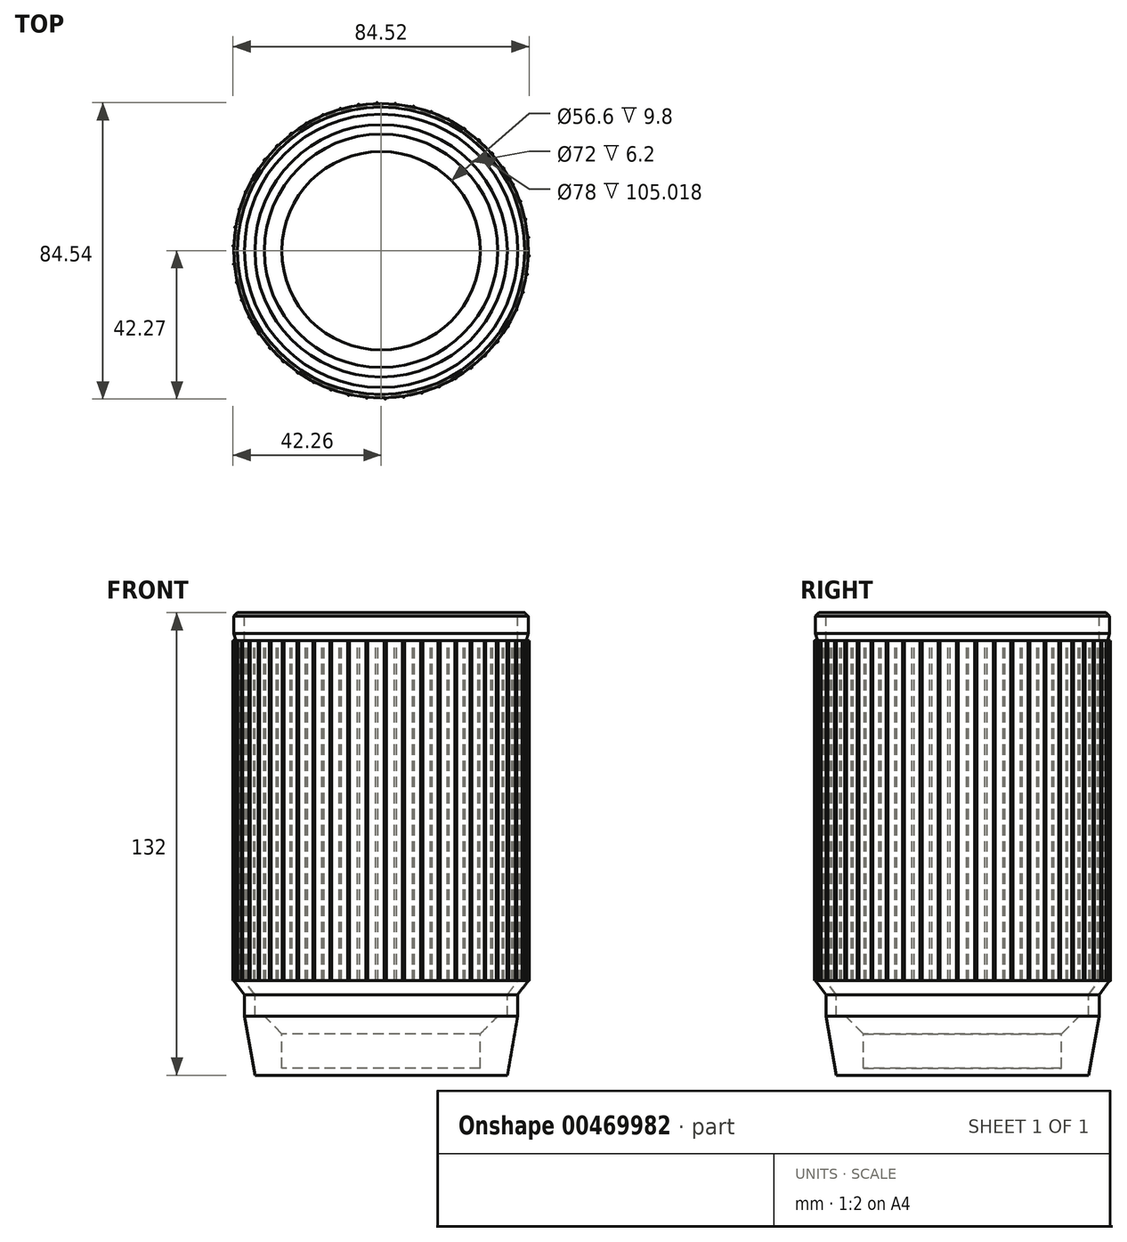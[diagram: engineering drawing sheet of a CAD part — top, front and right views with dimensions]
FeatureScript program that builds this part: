
annotation { "Feature Type Name" : "Feature", "Feature Type Description" : "" }
export const myFeature = defineFeature(function(context is Context, id is Id, definition is map)
    precondition{}
    {
        {
            var Q0;
            Q0=qCreatedBy(makeId("Front.planeOp"),FACE);
            var sketch = newSketch(context, id + "F0", { "sketchPlane" : qUnion([Q0])});
            skLineSegment(sketch, "E0", {"start": v(0, 0) * mm, "end": v(-28.3, 0) * mm});
            skLineSegment(sketch, "E1", {"start": v(-28.3, 0) * mm, "end": v(-28.3, 9.8) * mm});
            skLineSegment(sketch, "E2.bottom", {"start": v(0, 0) * mm, "end": v(-36, 0) * mm, "construction": true});
            skLineSegment(sketch, "E2.top", {"start": v(0, 21) * mm, "end": v(-36, 21) * mm, "construction": true});
            skLineSegment(sketch, "E2.left", {"start": v(0, 0) * mm, "end": v(0, 21) * mm, "construction": true});
            skLineSegment(sketch, "E2.right", {"start": v(-36, 0) * mm, "end": v(-36, 21) * mm, "construction": true});
            skLineSegment(sketch, "E3", {"start": v(-36, 21) * mm, "end": v(-36, 14.8) * mm});
            skLineSegment(sketch, "E4", {"start": v(-36, 14.8) * mm, "end": v(-33.3, 14.8) * mm});
            skLineSegment(sketch, "E5.bottom", {"start": v(0, 0) * mm, "end": v(-39, 0) * mm, "construction": true});
            skLineSegment(sketch, "E5.top", {"start": v(0, 130) * mm, "end": v(-39, 130) * mm, "construction": true});
            skLineSegment(sketch, "E5.left", {"start": v(0, 0) * mm, "end": v(0, 130) * mm, "construction": true});
            skLineSegment(sketch, "E5.right", {"start": v(-39, 0) * mm, "end": v(-39, 130) * mm, "construction": true});
            skLineSegment(sketch, "E6", {"start": v(-36, 21) * mm, "end": v(-39, 24.98) * mm});
            skLineSegment(sketch, "E7", {"start": v(-39, 24.98) * mm, "end": v(-39, 130) * mm});
            skLineSegment(sketch, "E8", {"start": v(-39, 130) * mm, "end": v(-42, 130) * mm});
            skLineSegment(sketch, "E9", {"start": v(-42, 130) * mm, "end": v(-42, 124) * mm});
            skLineSegment(sketch, "E10.bottom", {"start": v(-39, 130) * mm, "end": v(-41.4, 130) * mm, "construction": true});
            skLineSegment(sketch, "E10.top", {"start": v(-39, 122) * mm, "end": v(-41.4, 122) * mm, "construction": true});
            skLineSegment(sketch, "E10.left", {"start": v(-39, 130) * mm, "end": v(-39, 122) * mm, "construction": true});
            skLineSegment(sketch, "E10.right", {"start": v(-41.4, 130) * mm, "end": v(-41.4, 122) * mm, "construction": true});
            skLineSegment(sketch, "E11", {"start": v(-42, 124) * mm, "end": v(-41.4, 122) * mm});
            skLineSegment(sketch, "E12", {"start": v(-42, 122) * mm, "end": v(-42, 24.98) * mm});
            skLineSegment(sketch, "E13", {"start": v(-42, 24.98) * mm, "end": v(-39, 21) * mm});
            skLineSegment(sketch, "E14", {"start": v(-39, 21) * mm, "end": v(-39, 14.8) * mm});
            skLineSegment(sketch, "E15", {"start": v(-36, 17.9) * mm, "end": v(-39, 17.9) * mm, "construction": true});
            skLineSegment(sketch, "E16", {"start": v(0, 0) * mm, "end": v(0, -2) * mm});
            skLineSegment(sketch, "E17", {"start": v(0, -2) * mm, "end": v(-28.3, -2) * mm});
            skLineSegment(sketch, "E18", {"start": v(-39, 14.8) * mm, "end": v(-36, -2) * mm});
            skLineSegment(sketch, "E19", {"start": v(-36, -2) * mm, "end": v(-28.3, -2) * mm});
            skLineSegment(sketch, "E20", {"start": v(-33.3, 14.8) * mm, "end": v(-28.3, 9.8) * mm});
            skLineSegment(sketch, "E21", {"start": v(-42, 122) * mm, "end": v(-41.4, 122) * mm});
            skSolve(sketch);
        }
        {
            var Q0;
            Q0=makeQuery(id+"F0.imprint","IMPRINT",FACE,{"disambiguationData":[TD([[makeQuery(id+"F0.imprint","IMPRINT",EDGE,{"derivedFrom":sQuery(id+"F0.wireOp",EDGE,"E0")}),1.0]])]});
            var Q1;
            Q1=sQuery(id+"F0.wireOp",EDGE,"E16");
            revolve(context, id + "F1", {"entities" : qUnion([Q0]), "axis" : qUnion([Q1]), "revolveType" : RevolveType.FULL});
        }
        {
            var Q0;
            Q0=makeQuery(id+"F1.opRevolve","SWEPT_FACE",FACE,{"disambiguationData":[OSD([sQuery(id+"F0.wireOp",EDGE,"E21")])]});
            var sketch = newSketch(context, id + "F2", { "sketchPlane" : qUnion([Q0])});
            skCircle(sketch, "E22", {"center": v(36.08, -21.5) * mm, "radius": 0.29 * mm});
            skCircle(sketch, "E23.1.0", {"center": v(38.5, -16.8) * mm, "radius": 0.29 * mm});
            skCircle(sketch, "E23.2.0", {"center": v(40.3, -11.84) * mm, "radius": 0.29 * mm});
            skCircle(sketch, "E23.3.0", {"center": v(41.46, -6.7) * mm, "radius": 0.29 * mm});
            skCircle(sketch, "E23.4.0", {"center": v(41.97, -1.45) * mm, "radius": 0.29 * mm});
            skCircle(sketch, "E23.5.0", {"center": v(41.83, 3.82) * mm, "radius": 0.29 * mm});
            skCircle(sketch, "E23.6.0", {"center": v(41.02, 9.03) * mm, "radius": 0.29 * mm});
            skCircle(sketch, "E23.7.0", {"center": v(39.56, 14.1) * mm, "radius": 0.29 * mm});
            skCircle(sketch, "E23.8.0", {"center": v(37.48, 18.95) * mm, "radius": 0.29 * mm});
            skCircle(sketch, "E23.9.0", {"center": v(34.81, 23.5) * mm, "radius": 0.29 * mm});
            skCircle(sketch, "E23.10.0", {"center": v(31.6, 27.68) * mm, "radius": 0.29 * mm});
            skCircle(sketch, "E23.11.0", {"center": v(27.87, 31.42) * mm, "radius": 0.29 * mm});
            skCircle(sketch, "E23.12.0", {"center": v(23.72, 34.66) * mm, "radius": 0.29 * mm});
            skCircle(sketch, "E23.13.0", {"center": v(19.19, 37.36) * mm, "radius": 0.29 * mm});
            skCircle(sketch, "E23.14.0", {"center": v(14.35, 39.47) * mm, "radius": 0.29 * mm});
            skCircle(sketch, "E23.15.0", {"center": v(9.3, 40.96) * mm, "radius": 0.29 * mm});
            skCircle(sketch, "E23.16.0", {"center": v(4.08, 41.8) * mm, "radius": 0.29 * mm});
            skCircle(sketch, "E23.17.0", {"center": v(-1.19, 41.98) * mm, "radius": 0.29 * mm});
            skCircle(sketch, "E23.18.0", {"center": v(-6.44, 41.5) * mm, "radius": 0.29 * mm});
            skCircle(sketch, "E23.19.0", {"center": v(-11.6, 40.37) * mm, "radius": 0.29 * mm});
            skCircle(sketch, "E23.20.0", {"center": v(-16.56, 38.6) * mm, "radius": 0.29 * mm});
            skCircle(sketch, "E23.21.0", {"center": v(-21.27, 36.22) * mm, "radius": 0.29 * mm});
            skCircle(sketch, "E23.22.0", {"center": v(-25.64, 33.27) * mm, "radius": 0.29 * mm});
            skCircle(sketch, "E23.23.0", {"center": v(-29.6, 29.8) * mm, "radius": 0.29 * mm});
            skCircle(sketch, "E23.24.0", {"center": v(-33.1, 25.85) * mm, "radius": 0.29 * mm});
            skCircle(sketch, "E23.25.0", {"center": v(-36.08, 21.5) * mm, "radius": 0.29 * mm});
            skCircle(sketch, "E23.26.0", {"center": v(-38.5, 16.8) * mm, "radius": 0.29 * mm});
            skCircle(sketch, "E23.27.0", {"center": v(-40.3, 11.84) * mm, "radius": 0.29 * mm});
            skCircle(sketch, "E23.28.0", {"center": v(-41.46, 6.7) * mm, "radius": 0.29 * mm});
            skCircle(sketch, "E23.29.0", {"center": v(-41.97, 1.45) * mm, "radius": 0.29 * mm});
            skCircle(sketch, "E23.30.0", {"center": v(-41.83, -3.82) * mm, "radius": 0.29 * mm});
            skCircle(sketch, "E23.31.0", {"center": v(-41.02, -9.03) * mm, "radius": 0.29 * mm});
            skCircle(sketch, "E23.32.0", {"center": v(-39.56, -14.1) * mm, "radius": 0.29 * mm});
            skCircle(sketch, "E23.33.0", {"center": v(-37.48, -18.95) * mm, "radius": 0.29 * mm});
            skCircle(sketch, "E23.34.0", {"center": v(-34.81, -23.5) * mm, "radius": 0.29 * mm});
            skCircle(sketch, "E23.35.0", {"center": v(-31.6, -27.68) * mm, "radius": 0.29 * mm});
            skCircle(sketch, "E23.36.0", {"center": v(-27.87, -31.42) * mm, "radius": 0.29 * mm});
            skCircle(sketch, "E23.37.0", {"center": v(-23.72, -34.66) * mm, "radius": 0.29 * mm});
            skCircle(sketch, "E23.38.0", {"center": v(-19.19, -37.36) * mm, "radius": 0.29 * mm});
            skCircle(sketch, "E23.39.0", {"center": v(-14.35, -39.47) * mm, "radius": 0.29 * mm});
            skCircle(sketch, "E23.40.0", {"center": v(-9.3, -40.96) * mm, "radius": 0.29 * mm});
            skCircle(sketch, "E23.41.0", {"center": v(-4.08, -41.8) * mm, "radius": 0.29 * mm});
            skCircle(sketch, "E23.42.0", {"center": v(1.19, -41.98) * mm, "radius": 0.29 * mm});
            skCircle(sketch, "E23.43.0", {"center": v(6.44, -41.5) * mm, "radius": 0.29 * mm});
            skCircle(sketch, "E23.44.0", {"center": v(11.6, -40.37) * mm, "radius": 0.29 * mm});
            skCircle(sketch, "E23.45.0", {"center": v(16.56, -38.6) * mm, "radius": 0.29 * mm});
            skCircle(sketch, "E23.46.0", {"center": v(21.27, -36.22) * mm, "radius": 0.29 * mm});
            skCircle(sketch, "E23.47.0", {"center": v(25.64, -33.27) * mm, "radius": 0.29 * mm});
            skCircle(sketch, "E23.48.0", {"center": v(29.6, -29.8) * mm, "radius": 0.29 * mm});
            skCircle(sketch, "E23.49.0", {"center": v(33.1, -25.85) * mm, "radius": 0.29 * mm});
            skPoint(sketch, "E23.center", {"position": v(0, 0) * mm});
            skSolve(sketch);
        }
        {
            var Q0;
            {var subQ0=sQuery(id+"F2.wireOp",EDGE,"E23.46.0");var subQ1=makeQuery(id+"F1.opRevolve","SWEPT_EDGE",EDGE,{"disambiguationData":[OSD([sQuery(id+"F0.wireOp",EDGE,"E12"),sQuery(id+"F0.wireOp",EDGE,"E21")])]});var subQ2=makeQuery(id+"F2.imprint","INTERSECT",VERTEX,{"disambiguationData":[OD(0.0)],"derivedFrom":[subQ1,subQ0]});Q0=makeQuery(id+"F2.imprint","IMPRINT",FACE,{"disambiguationData":[TD([[makeQuery(id+"F2.imprint","IMPRINT",EDGE,{"disambiguationData":[TD([[subQ2,1.0]])],"derivedFrom":subQ0}),1.0]])]});}
            var Q1;
            {var subQ0=sQuery(id+"F2.wireOp",EDGE,"E23.46.0");var subQ1=makeQuery(id+"F1.opRevolve","SWEPT_EDGE",EDGE,{"disambiguationData":[OSD([sQuery(id+"F0.wireOp",EDGE,"E12"),sQuery(id+"F0.wireOp",EDGE,"E21")])]});var subQ2=makeQuery(id+"F2.imprint","INTERSECT",VERTEX,{"disambiguationData":[OD(0.0)],"derivedFrom":[subQ1,subQ0]});Q1=makeQuery(id+"F2.imprint","IMPRINT",FACE,{"disambiguationData":[TD([[makeQuery(id+"F2.imprint","IMPRINT",EDGE,{"disambiguationData":[TD([[subQ2,-1.0]])],"derivedFrom":subQ0}),1.0]])]});}
            var Q2;
            {var subQ0=sQuery(id+"F2.wireOp",EDGE,"E23.47.0");var subQ1=makeQuery(id+"F1.opRevolve","SWEPT_EDGE",EDGE,{"disambiguationData":[OSD([sQuery(id+"F0.wireOp",EDGE,"E12"),sQuery(id+"F0.wireOp",EDGE,"E21")])]});var subQ2=makeQuery(id+"F2.imprint","INTERSECT",VERTEX,{"disambiguationData":[OD(0.0)],"derivedFrom":[subQ1,subQ0]});Q2=makeQuery(id+"F2.imprint","IMPRINT",FACE,{"disambiguationData":[TD([[makeQuery(id+"F2.imprint","IMPRINT",EDGE,{"disambiguationData":[TD([[subQ2,-1.0]])],"derivedFrom":subQ0}),1.0]])]});}
            var Q3;
            {var subQ0=sQuery(id+"F2.wireOp",EDGE,"E23.47.0");var subQ1=makeQuery(id+"F1.opRevolve","SWEPT_EDGE",EDGE,{"disambiguationData":[OSD([sQuery(id+"F0.wireOp",EDGE,"E12"),sQuery(id+"F0.wireOp",EDGE,"E21")])]});var subQ2=makeQuery(id+"F2.imprint","INTERSECT",VERTEX,{"disambiguationData":[OD(0.0)],"derivedFrom":[subQ1,subQ0]});Q3=makeQuery(id+"F2.imprint","IMPRINT",FACE,{"disambiguationData":[TD([[makeQuery(id+"F2.imprint","IMPRINT",EDGE,{"disambiguationData":[TD([[subQ2,1.0]])],"derivedFrom":subQ0}),1.0]])]});}
            var Q4;
            {var subQ0=sQuery(id+"F2.wireOp",EDGE,"E23.48.0");var subQ1=makeQuery(id+"F1.opRevolve","SWEPT_EDGE",EDGE,{"disambiguationData":[OSD([sQuery(id+"F0.wireOp",EDGE,"E12"),sQuery(id+"F0.wireOp",EDGE,"E21")])]});var subQ2=makeQuery(id+"F2.imprint","INTERSECT",VERTEX,{"disambiguationData":[OD(0.0)],"derivedFrom":[subQ1,subQ0]});Q4=makeQuery(id+"F2.imprint","IMPRINT",FACE,{"disambiguationData":[TD([[makeQuery(id+"F2.imprint","IMPRINT",EDGE,{"disambiguationData":[TD([[subQ2,-1.0]])],"derivedFrom":subQ0}),1.0]])]});}
            var Q5;
            {var subQ0=sQuery(id+"F2.wireOp",EDGE,"E23.48.0");var subQ1=makeQuery(id+"F1.opRevolve","SWEPT_EDGE",EDGE,{"disambiguationData":[OSD([sQuery(id+"F0.wireOp",EDGE,"E12"),sQuery(id+"F0.wireOp",EDGE,"E21")])]});var subQ2=makeQuery(id+"F2.imprint","INTERSECT",VERTEX,{"disambiguationData":[OD(0.0)],"derivedFrom":[subQ1,subQ0]});Q5=makeQuery(id+"F2.imprint","IMPRINT",FACE,{"disambiguationData":[TD([[makeQuery(id+"F2.imprint","IMPRINT",EDGE,{"disambiguationData":[TD([[subQ2,1.0]])],"derivedFrom":subQ0}),1.0]])]});}
            var Q6;
            {var subQ0=sQuery(id+"F2.wireOp",EDGE,"E23.49.0");var subQ1=makeQuery(id+"F1.opRevolve","SWEPT_EDGE",EDGE,{"disambiguationData":[OSD([sQuery(id+"F0.wireOp",EDGE,"E12"),sQuery(id+"F0.wireOp",EDGE,"E21")])]});var subQ2=makeQuery(id+"F2.imprint","INTERSECT",VERTEX,{"disambiguationData":[OD(0.0)],"derivedFrom":[subQ1,subQ0]});Q6=makeQuery(id+"F2.imprint","IMPRINT",FACE,{"disambiguationData":[TD([[makeQuery(id+"F2.imprint","IMPRINT",EDGE,{"disambiguationData":[TD([[subQ2,-1.0]])],"derivedFrom":subQ0}),1.0]])]});}
            var Q7;
            {var subQ0=sQuery(id+"F2.wireOp",EDGE,"E23.49.0");var subQ1=makeQuery(id+"F1.opRevolve","SWEPT_EDGE",EDGE,{"disambiguationData":[OSD([sQuery(id+"F0.wireOp",EDGE,"E12"),sQuery(id+"F0.wireOp",EDGE,"E21")])]});var subQ2=makeQuery(id+"F2.imprint","INTERSECT",VERTEX,{"disambiguationData":[OD(0.0)],"derivedFrom":[subQ1,subQ0]});Q7=makeQuery(id+"F2.imprint","IMPRINT",FACE,{"disambiguationData":[TD([[makeQuery(id+"F2.imprint","IMPRINT",EDGE,{"disambiguationData":[TD([[subQ2,1.0]])],"derivedFrom":subQ0}),1.0]])]});}
            var Q8;
            {var subQ0=sQuery(id+"F2.wireOp",EDGE,"E22");var subQ1=makeQuery(id+"F1.opRevolve","SWEPT_EDGE",EDGE,{"disambiguationData":[OSD([sQuery(id+"F0.wireOp",EDGE,"E12"),sQuery(id+"F0.wireOp",EDGE,"E21")])]});var subQ2=makeQuery(id+"F2.imprint","INTERSECT",VERTEX,{"disambiguationData":[OD(0.0)],"derivedFrom":[subQ1,subQ0]});Q8=makeQuery(id+"F2.imprint","IMPRINT",FACE,{"disambiguationData":[TD([[makeQuery(id+"F2.imprint","IMPRINT",EDGE,{"disambiguationData":[TD([[subQ2,-1.0]])],"derivedFrom":subQ0}),1.0]])]});}
            var Q9;
            {var subQ0=sQuery(id+"F2.wireOp",EDGE,"E22");var subQ1=makeQuery(id+"F1.opRevolve","SWEPT_EDGE",EDGE,{"disambiguationData":[OSD([sQuery(id+"F0.wireOp",EDGE,"E12"),sQuery(id+"F0.wireOp",EDGE,"E21")])]});var subQ2=makeQuery(id+"F2.imprint","INTERSECT",VERTEX,{"disambiguationData":[OD(0.0)],"derivedFrom":[subQ1,subQ0]});Q9=makeQuery(id+"F2.imprint","IMPRINT",FACE,{"disambiguationData":[TD([[makeQuery(id+"F2.imprint","IMPRINT",EDGE,{"disambiguationData":[TD([[subQ2,1.0]])],"derivedFrom":subQ0}),1.0]])]});}
            var Q10;
            {var subQ0=sQuery(id+"F2.wireOp",EDGE,"E23.1.0");var subQ1=makeQuery(id+"F1.opRevolve","SWEPT_EDGE",EDGE,{"disambiguationData":[OSD([sQuery(id+"F0.wireOp",EDGE,"E12"),sQuery(id+"F0.wireOp",EDGE,"E21")])]});var subQ2=makeQuery(id+"F2.imprint","INTERSECT",VERTEX,{"disambiguationData":[OD(0.0)],"derivedFrom":[subQ1,subQ0]});Q10=makeQuery(id+"F2.imprint","IMPRINT",FACE,{"disambiguationData":[TD([[makeQuery(id+"F2.imprint","IMPRINT",EDGE,{"disambiguationData":[TD([[subQ2,-1.0]])],"derivedFrom":subQ0}),1.0]])]});}
            var Q11;
            {var subQ0=sQuery(id+"F2.wireOp",EDGE,"E23.1.0");var subQ1=makeQuery(id+"F1.opRevolve","SWEPT_EDGE",EDGE,{"disambiguationData":[OSD([sQuery(id+"F0.wireOp",EDGE,"E12"),sQuery(id+"F0.wireOp",EDGE,"E21")])]});var subQ2=makeQuery(id+"F2.imprint","INTERSECT",VERTEX,{"disambiguationData":[OD(0.0)],"derivedFrom":[subQ1,subQ0]});Q11=makeQuery(id+"F2.imprint","IMPRINT",FACE,{"disambiguationData":[TD([[makeQuery(id+"F2.imprint","IMPRINT",EDGE,{"disambiguationData":[TD([[subQ2,1.0]])],"derivedFrom":subQ0}),1.0]])]});}
            var Q12;
            {var subQ0=sQuery(id+"F2.wireOp",EDGE,"E23.2.0");var subQ1=makeQuery(id+"F1.opRevolve","SWEPT_EDGE",EDGE,{"disambiguationData":[OSD([sQuery(id+"F0.wireOp",EDGE,"E12"),sQuery(id+"F0.wireOp",EDGE,"E21")])]});var subQ2=makeQuery(id+"F2.imprint","INTERSECT",VERTEX,{"disambiguationData":[OD(0.0)],"derivedFrom":[subQ1,subQ0]});Q12=makeQuery(id+"F2.imprint","IMPRINT",FACE,{"disambiguationData":[TD([[makeQuery(id+"F2.imprint","IMPRINT",EDGE,{"disambiguationData":[TD([[subQ2,1.0]])],"derivedFrom":subQ0}),1.0]])]});}
            var Q13;
            {var subQ0=sQuery(id+"F2.wireOp",EDGE,"E23.2.0");var subQ1=makeQuery(id+"F1.opRevolve","SWEPT_EDGE",EDGE,{"disambiguationData":[OSD([sQuery(id+"F0.wireOp",EDGE,"E12"),sQuery(id+"F0.wireOp",EDGE,"E21")])]});var subQ2=makeQuery(id+"F2.imprint","INTERSECT",VERTEX,{"disambiguationData":[OD(0.0)],"derivedFrom":[subQ1,subQ0]});Q13=makeQuery(id+"F2.imprint","IMPRINT",FACE,{"disambiguationData":[TD([[makeQuery(id+"F2.imprint","IMPRINT",EDGE,{"disambiguationData":[TD([[subQ2,-1.0]])],"derivedFrom":subQ0}),1.0]])]});}
            var Q14;
            {var subQ0=sQuery(id+"F2.wireOp",EDGE,"E23.3.0");var subQ1=makeQuery(id+"F1.opRevolve","SWEPT_EDGE",EDGE,{"disambiguationData":[OSD([sQuery(id+"F0.wireOp",EDGE,"E12"),sQuery(id+"F0.wireOp",EDGE,"E21")])]});var subQ2=makeQuery(id+"F2.imprint","INTERSECT",VERTEX,{"disambiguationData":[OD(0.0)],"derivedFrom":[subQ1,subQ0]});Q14=makeQuery(id+"F2.imprint","IMPRINT",FACE,{"disambiguationData":[TD([[makeQuery(id+"F2.imprint","IMPRINT",EDGE,{"disambiguationData":[TD([[subQ2,1.0]])],"derivedFrom":subQ0}),1.0]])]});}
            var Q15;
            {var subQ0=sQuery(id+"F2.wireOp",EDGE,"E23.3.0");var subQ1=makeQuery(id+"F1.opRevolve","SWEPT_EDGE",EDGE,{"disambiguationData":[OSD([sQuery(id+"F0.wireOp",EDGE,"E12"),sQuery(id+"F0.wireOp",EDGE,"E21")])]});var subQ2=makeQuery(id+"F2.imprint","INTERSECT",VERTEX,{"disambiguationData":[OD(0.0)],"derivedFrom":[subQ1,subQ0]});Q15=makeQuery(id+"F2.imprint","IMPRINT",FACE,{"disambiguationData":[TD([[makeQuery(id+"F2.imprint","IMPRINT",EDGE,{"disambiguationData":[TD([[subQ2,-1.0]])],"derivedFrom":subQ0}),1.0]])]});}
            var Q16;
            {var subQ0=sQuery(id+"F2.wireOp",EDGE,"E23.4.0");var subQ1=makeQuery(id+"F1.opRevolve","SWEPT_EDGE",EDGE,{"disambiguationData":[OSD([sQuery(id+"F0.wireOp",EDGE,"E12"),sQuery(id+"F0.wireOp",EDGE,"E21")])]});var subQ2=makeQuery(id+"F2.imprint","INTERSECT",VERTEX,{"disambiguationData":[OD(0.0)],"derivedFrom":[subQ1,subQ0]});Q16=makeQuery(id+"F2.imprint","IMPRINT",FACE,{"disambiguationData":[TD([[makeQuery(id+"F2.imprint","IMPRINT",EDGE,{"disambiguationData":[TD([[subQ2,-1.0]])],"derivedFrom":subQ0}),1.0]])]});}
            var Q17;
            {var subQ0=sQuery(id+"F2.wireOp",EDGE,"E23.5.0");var subQ1=makeQuery(id+"F1.opRevolve","SWEPT_EDGE",EDGE,{"disambiguationData":[OSD([sQuery(id+"F0.wireOp",EDGE,"E12"),sQuery(id+"F0.wireOp",EDGE,"E21")])]});var subQ2=makeQuery(id+"F2.imprint","INTERSECT",VERTEX,{"disambiguationData":[OD(0.0)],"derivedFrom":[subQ1,subQ0]});Q17=makeQuery(id+"F2.imprint","IMPRINT",FACE,{"disambiguationData":[TD([[makeQuery(id+"F2.imprint","IMPRINT",EDGE,{"disambiguationData":[TD([[subQ2,-1.0]])],"derivedFrom":subQ0}),1.0]])]});}
            var Q18;
            {var subQ0=sQuery(id+"F2.wireOp",EDGE,"E23.9.0");var subQ1=makeQuery(id+"F1.opRevolve","SWEPT_EDGE",EDGE,{"disambiguationData":[OSD([sQuery(id+"F0.wireOp",EDGE,"E12"),sQuery(id+"F0.wireOp",EDGE,"E21")])]});var subQ2=makeQuery(id+"F2.imprint","INTERSECT",VERTEX,{"disambiguationData":[OD(0.0)],"derivedFrom":[subQ1,subQ0]});Q18=makeQuery(id+"F2.imprint","IMPRINT",FACE,{"disambiguationData":[TD([[makeQuery(id+"F2.imprint","IMPRINT",EDGE,{"disambiguationData":[TD([[subQ2,1.0]])],"derivedFrom":subQ0}),1.0]])]});}
            var Q19;
            {var subQ0=sQuery(id+"F2.wireOp",EDGE,"E23.8.0");var subQ1=makeQuery(id+"F1.opRevolve","SWEPT_EDGE",EDGE,{"disambiguationData":[OSD([sQuery(id+"F0.wireOp",EDGE,"E12"),sQuery(id+"F0.wireOp",EDGE,"E21")])]});var subQ2=makeQuery(id+"F2.imprint","INTERSECT",VERTEX,{"disambiguationData":[OD(0.0)],"derivedFrom":[subQ1,subQ0]});Q19=makeQuery(id+"F2.imprint","IMPRINT",FACE,{"disambiguationData":[TD([[makeQuery(id+"F2.imprint","IMPRINT",EDGE,{"disambiguationData":[TD([[subQ2,1.0]])],"derivedFrom":subQ0}),1.0]])]});}
            var Q20;
            {var subQ0=sQuery(id+"F2.wireOp",EDGE,"E23.7.0");var subQ1=makeQuery(id+"F1.opRevolve","SWEPT_EDGE",EDGE,{"disambiguationData":[OSD([sQuery(id+"F0.wireOp",EDGE,"E12"),sQuery(id+"F0.wireOp",EDGE,"E21")])]});var subQ2=makeQuery(id+"F2.imprint","INTERSECT",VERTEX,{"disambiguationData":[OD(0.0)],"derivedFrom":[subQ1,subQ0]});Q20=makeQuery(id+"F2.imprint","IMPRINT",FACE,{"disambiguationData":[TD([[makeQuery(id+"F2.imprint","IMPRINT",EDGE,{"disambiguationData":[TD([[subQ2,-1.0]])],"derivedFrom":subQ0}),1.0]])]});}
            var Q21;
            {var subQ0=sQuery(id+"F2.wireOp",EDGE,"E23.6.0");var subQ1=makeQuery(id+"F1.opRevolve","SWEPT_EDGE",EDGE,{"disambiguationData":[OSD([sQuery(id+"F0.wireOp",EDGE,"E12"),sQuery(id+"F0.wireOp",EDGE,"E21")])]});var subQ2=makeQuery(id+"F2.imprint","INTERSECT",VERTEX,{"disambiguationData":[OD(0.0)],"derivedFrom":[subQ1,subQ0]});Q21=makeQuery(id+"F2.imprint","IMPRINT",FACE,{"disambiguationData":[TD([[makeQuery(id+"F2.imprint","IMPRINT",EDGE,{"disambiguationData":[TD([[subQ2,-1.0]])],"derivedFrom":subQ0}),1.0]])]});}
            var Q22;
            {var subQ0=sQuery(id+"F2.wireOp",EDGE,"E23.7.0");var subQ1=makeQuery(id+"F1.opRevolve","SWEPT_EDGE",EDGE,{"disambiguationData":[OSD([sQuery(id+"F0.wireOp",EDGE,"E12"),sQuery(id+"F0.wireOp",EDGE,"E21")])]});var subQ2=makeQuery(id+"F2.imprint","INTERSECT",VERTEX,{"disambiguationData":[OD(0.0)],"derivedFrom":[subQ1,subQ0]});Q22=makeQuery(id+"F2.imprint","IMPRINT",FACE,{"disambiguationData":[TD([[makeQuery(id+"F2.imprint","IMPRINT",EDGE,{"disambiguationData":[TD([[subQ2,1.0]])],"derivedFrom":subQ0}),1.0]])]});}
            var Q23;
            {var subQ0=sQuery(id+"F2.wireOp",EDGE,"E23.8.0");var subQ1=makeQuery(id+"F1.opRevolve","SWEPT_EDGE",EDGE,{"disambiguationData":[OSD([sQuery(id+"F0.wireOp",EDGE,"E12"),sQuery(id+"F0.wireOp",EDGE,"E21")])]});var subQ2=makeQuery(id+"F2.imprint","INTERSECT",VERTEX,{"disambiguationData":[OD(0.0)],"derivedFrom":[subQ1,subQ0]});Q23=makeQuery(id+"F2.imprint","IMPRINT",FACE,{"disambiguationData":[TD([[makeQuery(id+"F2.imprint","IMPRINT",EDGE,{"disambiguationData":[TD([[subQ2,-1.0]])],"derivedFrom":subQ0}),1.0]])]});}
            var Q24;
            {var subQ0=sQuery(id+"F2.wireOp",EDGE,"E23.6.0");var subQ1=makeQuery(id+"F1.opRevolve","SWEPT_EDGE",EDGE,{"disambiguationData":[OSD([sQuery(id+"F0.wireOp",EDGE,"E12"),sQuery(id+"F0.wireOp",EDGE,"E21")])]});var subQ2=makeQuery(id+"F2.imprint","INTERSECT",VERTEX,{"disambiguationData":[OD(0.0)],"derivedFrom":[subQ1,subQ0]});Q24=makeQuery(id+"F2.imprint","IMPRINT",FACE,{"disambiguationData":[TD([[makeQuery(id+"F2.imprint","IMPRINT",EDGE,{"disambiguationData":[TD([[subQ2,1.0]])],"derivedFrom":subQ0}),1.0]])]});}
            var Q25;
            {var subQ0=sQuery(id+"F2.wireOp",EDGE,"E23.5.0");var subQ1=makeQuery(id+"F1.opRevolve","SWEPT_EDGE",EDGE,{"disambiguationData":[OSD([sQuery(id+"F0.wireOp",EDGE,"E12"),sQuery(id+"F0.wireOp",EDGE,"E21")])]});var subQ2=makeQuery(id+"F2.imprint","INTERSECT",VERTEX,{"disambiguationData":[OD(0.0)],"derivedFrom":[subQ1,subQ0]});Q25=makeQuery(id+"F2.imprint","IMPRINT",FACE,{"disambiguationData":[TD([[makeQuery(id+"F2.imprint","IMPRINT",EDGE,{"disambiguationData":[TD([[subQ2,1.0]])],"derivedFrom":subQ0}),1.0]])]});}
            var Q26;
            {var subQ0=sQuery(id+"F2.wireOp",EDGE,"E23.4.0");var subQ1=makeQuery(id+"F1.opRevolve","SWEPT_EDGE",EDGE,{"disambiguationData":[OSD([sQuery(id+"F0.wireOp",EDGE,"E12"),sQuery(id+"F0.wireOp",EDGE,"E21")])]});var subQ2=makeQuery(id+"F2.imprint","INTERSECT",VERTEX,{"disambiguationData":[OD(0.0)],"derivedFrom":[subQ1,subQ0]});Q26=makeQuery(id+"F2.imprint","IMPRINT",FACE,{"disambiguationData":[TD([[makeQuery(id+"F2.imprint","IMPRINT",EDGE,{"disambiguationData":[TD([[subQ2,1.0]])],"derivedFrom":subQ0}),1.0]])]});}
            var Q27;
            {var subQ0=sQuery(id+"F2.wireOp",EDGE,"E23.9.0");var subQ1=makeQuery(id+"F1.opRevolve","SWEPT_EDGE",EDGE,{"disambiguationData":[OSD([sQuery(id+"F0.wireOp",EDGE,"E12"),sQuery(id+"F0.wireOp",EDGE,"E21")])]});var subQ2=makeQuery(id+"F2.imprint","INTERSECT",VERTEX,{"disambiguationData":[OD(0.0)],"derivedFrom":[subQ1,subQ0]});Q27=makeQuery(id+"F2.imprint","IMPRINT",FACE,{"disambiguationData":[TD([[makeQuery(id+"F2.imprint","IMPRINT",EDGE,{"disambiguationData":[TD([[subQ2,-1.0]])],"derivedFrom":subQ0}),1.0]])]});}
            var Q28;
            {var subQ0=sQuery(id+"F2.wireOp",EDGE,"E23.11.0");var subQ1=makeQuery(id+"F1.opRevolve","SWEPT_EDGE",EDGE,{"disambiguationData":[OSD([sQuery(id+"F0.wireOp",EDGE,"E12"),sQuery(id+"F0.wireOp",EDGE,"E21")])]});var subQ2=makeQuery(id+"F2.imprint","INTERSECT",VERTEX,{"disambiguationData":[OD(0.0)],"derivedFrom":[subQ1,subQ0]});Q28=makeQuery(id+"F2.imprint","IMPRINT",FACE,{"disambiguationData":[TD([[makeQuery(id+"F2.imprint","IMPRINT",EDGE,{"disambiguationData":[TD([[subQ2,1.0]])],"derivedFrom":subQ0}),1.0]])]});}
            var Q29;
            {var subQ0=sQuery(id+"F2.wireOp",EDGE,"E23.11.0");var subQ1=makeQuery(id+"F1.opRevolve","SWEPT_EDGE",EDGE,{"disambiguationData":[OSD([sQuery(id+"F0.wireOp",EDGE,"E12"),sQuery(id+"F0.wireOp",EDGE,"E21")])]});var subQ2=makeQuery(id+"F2.imprint","INTERSECT",VERTEX,{"disambiguationData":[OD(0.0)],"derivedFrom":[subQ1,subQ0]});Q29=makeQuery(id+"F2.imprint","IMPRINT",FACE,{"disambiguationData":[TD([[makeQuery(id+"F2.imprint","IMPRINT",EDGE,{"disambiguationData":[TD([[subQ2,-1.0]])],"derivedFrom":subQ0}),1.0]])]});}
            var Q30;
            {var subQ0=sQuery(id+"F2.wireOp",EDGE,"E23.10.0");var subQ1=makeQuery(id+"F1.opRevolve","SWEPT_EDGE",EDGE,{"disambiguationData":[OSD([sQuery(id+"F0.wireOp",EDGE,"E12"),sQuery(id+"F0.wireOp",EDGE,"E21")])]});var subQ2=makeQuery(id+"F2.imprint","INTERSECT",VERTEX,{"disambiguationData":[OD(0.0)],"derivedFrom":[subQ1,subQ0]});Q30=makeQuery(id+"F2.imprint","IMPRINT",FACE,{"disambiguationData":[TD([[makeQuery(id+"F2.imprint","IMPRINT",EDGE,{"disambiguationData":[TD([[subQ2,-1.0]])],"derivedFrom":subQ0}),1.0]])]});}
            var Q31;
            {var subQ0=sQuery(id+"F2.wireOp",EDGE,"E23.10.0");var subQ1=makeQuery(id+"F1.opRevolve","SWEPT_EDGE",EDGE,{"disambiguationData":[OSD([sQuery(id+"F0.wireOp",EDGE,"E12"),sQuery(id+"F0.wireOp",EDGE,"E21")])]});var subQ2=makeQuery(id+"F2.imprint","INTERSECT",VERTEX,{"disambiguationData":[OD(0.0)],"derivedFrom":[subQ1,subQ0]});Q31=makeQuery(id+"F2.imprint","IMPRINT",FACE,{"disambiguationData":[TD([[makeQuery(id+"F2.imprint","IMPRINT",EDGE,{"disambiguationData":[TD([[subQ2,1.0]])],"derivedFrom":subQ0}),1.0]])]});}
            var Q32;
            {var subQ0=sQuery(id+"F2.wireOp",EDGE,"E23.12.0");var subQ1=makeQuery(id+"F1.opRevolve","SWEPT_EDGE",EDGE,{"disambiguationData":[OSD([sQuery(id+"F0.wireOp",EDGE,"E12"),sQuery(id+"F0.wireOp",EDGE,"E21")])]});var subQ2=makeQuery(id+"F2.imprint","INTERSECT",VERTEX,{"disambiguationData":[OD(0.0)],"derivedFrom":[subQ1,subQ0]});Q32=makeQuery(id+"F2.imprint","IMPRINT",FACE,{"disambiguationData":[TD([[makeQuery(id+"F2.imprint","IMPRINT",EDGE,{"disambiguationData":[TD([[subQ2,-1.0]])],"derivedFrom":subQ0}),1.0]])]});}
            var Q33;
            {var subQ0=sQuery(id+"F2.wireOp",EDGE,"E23.12.0");var subQ1=makeQuery(id+"F1.opRevolve","SWEPT_EDGE",EDGE,{"disambiguationData":[OSD([sQuery(id+"F0.wireOp",EDGE,"E12"),sQuery(id+"F0.wireOp",EDGE,"E21")])]});var subQ2=makeQuery(id+"F2.imprint","INTERSECT",VERTEX,{"disambiguationData":[OD(0.0)],"derivedFrom":[subQ1,subQ0]});Q33=makeQuery(id+"F2.imprint","IMPRINT",FACE,{"disambiguationData":[TD([[makeQuery(id+"F2.imprint","IMPRINT",EDGE,{"disambiguationData":[TD([[subQ2,1.0]])],"derivedFrom":subQ0}),1.0]])]});}
            var Q34;
            {var subQ0=sQuery(id+"F2.wireOp",EDGE,"E23.13.0");var subQ1=makeQuery(id+"F1.opRevolve","SWEPT_EDGE",EDGE,{"disambiguationData":[OSD([sQuery(id+"F0.wireOp",EDGE,"E12"),sQuery(id+"F0.wireOp",EDGE,"E21")])]});var subQ2=makeQuery(id+"F2.imprint","INTERSECT",VERTEX,{"disambiguationData":[OD(0.0)],"derivedFrom":[subQ1,subQ0]});Q34=makeQuery(id+"F2.imprint","IMPRINT",FACE,{"disambiguationData":[TD([[makeQuery(id+"F2.imprint","IMPRINT",EDGE,{"disambiguationData":[TD([[subQ2,-1.0]])],"derivedFrom":subQ0}),1.0]])]});}
            var Q35;
            {var subQ0=sQuery(id+"F2.wireOp",EDGE,"E23.13.0");var subQ1=makeQuery(id+"F1.opRevolve","SWEPT_EDGE",EDGE,{"disambiguationData":[OSD([sQuery(id+"F0.wireOp",EDGE,"E12"),sQuery(id+"F0.wireOp",EDGE,"E21")])]});var subQ2=makeQuery(id+"F2.imprint","INTERSECT",VERTEX,{"disambiguationData":[OD(0.0)],"derivedFrom":[subQ1,subQ0]});Q35=makeQuery(id+"F2.imprint","IMPRINT",FACE,{"disambiguationData":[TD([[makeQuery(id+"F2.imprint","IMPRINT",EDGE,{"disambiguationData":[TD([[subQ2,1.0]])],"derivedFrom":subQ0}),1.0]])]});}
            var Q36;
            {var subQ0=sQuery(id+"F2.wireOp",EDGE,"E23.14.0");var subQ1=makeQuery(id+"F1.opRevolve","SWEPT_EDGE",EDGE,{"disambiguationData":[OSD([sQuery(id+"F0.wireOp",EDGE,"E12"),sQuery(id+"F0.wireOp",EDGE,"E21")])]});var subQ2=makeQuery(id+"F2.imprint","INTERSECT",VERTEX,{"disambiguationData":[OD(0.0)],"derivedFrom":[subQ1,subQ0]});Q36=makeQuery(id+"F2.imprint","IMPRINT",FACE,{"disambiguationData":[TD([[makeQuery(id+"F2.imprint","IMPRINT",EDGE,{"disambiguationData":[TD([[subQ2,-1.0]])],"derivedFrom":subQ0}),1.0]])]});}
            var Q37;
            {var subQ0=sQuery(id+"F2.wireOp",EDGE,"E23.14.0");var subQ1=makeQuery(id+"F1.opRevolve","SWEPT_EDGE",EDGE,{"disambiguationData":[OSD([sQuery(id+"F0.wireOp",EDGE,"E12"),sQuery(id+"F0.wireOp",EDGE,"E21")])]});var subQ2=makeQuery(id+"F2.imprint","INTERSECT",VERTEX,{"disambiguationData":[OD(0.0)],"derivedFrom":[subQ1,subQ0]});Q37=makeQuery(id+"F2.imprint","IMPRINT",FACE,{"disambiguationData":[TD([[makeQuery(id+"F2.imprint","IMPRINT",EDGE,{"disambiguationData":[TD([[subQ2,1.0]])],"derivedFrom":subQ0}),1.0]])]});}
            var Q38;
            {var subQ0=sQuery(id+"F2.wireOp",EDGE,"E23.15.0");var subQ1=makeQuery(id+"F1.opRevolve","SWEPT_EDGE",EDGE,{"disambiguationData":[OSD([sQuery(id+"F0.wireOp",EDGE,"E12"),sQuery(id+"F0.wireOp",EDGE,"E21")])]});var subQ2=makeQuery(id+"F2.imprint","INTERSECT",VERTEX,{"disambiguationData":[OD(0.0)],"derivedFrom":[subQ1,subQ0]});Q38=makeQuery(id+"F2.imprint","IMPRINT",FACE,{"disambiguationData":[TD([[makeQuery(id+"F2.imprint","IMPRINT",EDGE,{"disambiguationData":[TD([[subQ2,-1.0]])],"derivedFrom":subQ0}),1.0]])]});}
            var Q39;
            {var subQ0=sQuery(id+"F2.wireOp",EDGE,"E23.15.0");var subQ1=makeQuery(id+"F1.opRevolve","SWEPT_EDGE",EDGE,{"disambiguationData":[OSD([sQuery(id+"F0.wireOp",EDGE,"E12"),sQuery(id+"F0.wireOp",EDGE,"E21")])]});var subQ2=makeQuery(id+"F2.imprint","INTERSECT",VERTEX,{"disambiguationData":[OD(0.0)],"derivedFrom":[subQ1,subQ0]});Q39=makeQuery(id+"F2.imprint","IMPRINT",FACE,{"disambiguationData":[TD([[makeQuery(id+"F2.imprint","IMPRINT",EDGE,{"disambiguationData":[TD([[subQ2,1.0]])],"derivedFrom":subQ0}),1.0]])]});}
            var Q40;
            {var subQ0=sQuery(id+"F2.wireOp",EDGE,"E23.17.0");var subQ1=makeQuery(id+"F1.opRevolve","SWEPT_EDGE",EDGE,{"disambiguationData":[OSD([sQuery(id+"F0.wireOp",EDGE,"E12"),sQuery(id+"F0.wireOp",EDGE,"E21")])]});var subQ2=makeQuery(id+"F2.imprint","INTERSECT",VERTEX,{"disambiguationData":[OD(0.0)],"derivedFrom":[subQ1,subQ0]});Q40=makeQuery(id+"F2.imprint","IMPRINT",FACE,{"disambiguationData":[TD([[makeQuery(id+"F2.imprint","IMPRINT",EDGE,{"disambiguationData":[TD([[subQ2,-1.0]])],"derivedFrom":subQ0}),1.0]])]});}
            var Q41;
            {var subQ0=sQuery(id+"F2.wireOp",EDGE,"E23.17.0");var subQ1=makeQuery(id+"F1.opRevolve","SWEPT_EDGE",EDGE,{"disambiguationData":[OSD([sQuery(id+"F0.wireOp",EDGE,"E12"),sQuery(id+"F0.wireOp",EDGE,"E21")])]});var subQ2=makeQuery(id+"F2.imprint","INTERSECT",VERTEX,{"disambiguationData":[OD(0.0)],"derivedFrom":[subQ1,subQ0]});Q41=makeQuery(id+"F2.imprint","IMPRINT",FACE,{"disambiguationData":[TD([[makeQuery(id+"F2.imprint","IMPRINT",EDGE,{"disambiguationData":[TD([[subQ2,1.0]])],"derivedFrom":subQ0}),1.0]])]});}
            var Q42;
            {var subQ0=sQuery(id+"F2.wireOp",EDGE,"E23.16.0");var subQ1=makeQuery(id+"F1.opRevolve","SWEPT_EDGE",EDGE,{"disambiguationData":[OSD([sQuery(id+"F0.wireOp",EDGE,"E12"),sQuery(id+"F0.wireOp",EDGE,"E21")])]});var subQ2=makeQuery(id+"F2.imprint","INTERSECT",VERTEX,{"disambiguationData":[OD(0.0)],"derivedFrom":[subQ1,subQ0]});Q42=makeQuery(id+"F2.imprint","IMPRINT",FACE,{"disambiguationData":[TD([[makeQuery(id+"F2.imprint","IMPRINT",EDGE,{"disambiguationData":[TD([[subQ2,-1.0]])],"derivedFrom":subQ0}),1.0]])]});}
            var Q43;
            {var subQ0=sQuery(id+"F2.wireOp",EDGE,"E23.16.0");var subQ1=makeQuery(id+"F1.opRevolve","SWEPT_EDGE",EDGE,{"disambiguationData":[OSD([sQuery(id+"F0.wireOp",EDGE,"E12"),sQuery(id+"F0.wireOp",EDGE,"E21")])]});var subQ2=makeQuery(id+"F2.imprint","INTERSECT",VERTEX,{"disambiguationData":[OD(0.0)],"derivedFrom":[subQ1,subQ0]});Q43=makeQuery(id+"F2.imprint","IMPRINT",FACE,{"disambiguationData":[TD([[makeQuery(id+"F2.imprint","IMPRINT",EDGE,{"disambiguationData":[TD([[subQ2,1.0]])],"derivedFrom":subQ0}),1.0]])]});}
            var Q44;
            {var subQ0=sQuery(id+"F2.wireOp",EDGE,"E23.20.0");var subQ1=makeQuery(id+"F1.opRevolve","SWEPT_EDGE",EDGE,{"disambiguationData":[OSD([sQuery(id+"F0.wireOp",EDGE,"E12"),sQuery(id+"F0.wireOp",EDGE,"E21")])]});var subQ2=makeQuery(id+"F2.imprint","INTERSECT",VERTEX,{"disambiguationData":[OD(0.0)],"derivedFrom":[subQ1,subQ0]});Q44=makeQuery(id+"F2.imprint","IMPRINT",FACE,{"disambiguationData":[TD([[makeQuery(id+"F2.imprint","IMPRINT",EDGE,{"disambiguationData":[TD([[subQ2,-1.0]])],"derivedFrom":subQ0}),1.0]])]});}
            var Q45;
            {var subQ0=sQuery(id+"F2.wireOp",EDGE,"E23.20.0");var subQ1=makeQuery(id+"F1.opRevolve","SWEPT_EDGE",EDGE,{"disambiguationData":[OSD([sQuery(id+"F0.wireOp",EDGE,"E12"),sQuery(id+"F0.wireOp",EDGE,"E21")])]});var subQ2=makeQuery(id+"F2.imprint","INTERSECT",VERTEX,{"disambiguationData":[OD(0.0)],"derivedFrom":[subQ1,subQ0]});Q45=makeQuery(id+"F2.imprint","IMPRINT",FACE,{"disambiguationData":[TD([[makeQuery(id+"F2.imprint","IMPRINT",EDGE,{"disambiguationData":[TD([[subQ2,1.0]])],"derivedFrom":subQ0}),1.0]])]});}
            var Q46;
            {var subQ0=sQuery(id+"F2.wireOp",EDGE,"E23.19.0");var subQ1=makeQuery(id+"F1.opRevolve","SWEPT_EDGE",EDGE,{"disambiguationData":[OSD([sQuery(id+"F0.wireOp",EDGE,"E12"),sQuery(id+"F0.wireOp",EDGE,"E21")])]});var subQ2=makeQuery(id+"F2.imprint","INTERSECT",VERTEX,{"disambiguationData":[OD(0.0)],"derivedFrom":[subQ1,subQ0]});Q46=makeQuery(id+"F2.imprint","IMPRINT",FACE,{"disambiguationData":[TD([[makeQuery(id+"F2.imprint","IMPRINT",EDGE,{"disambiguationData":[TD([[subQ2,-1.0]])],"derivedFrom":subQ0}),1.0]])]});}
            var Q47;
            {var subQ0=sQuery(id+"F2.wireOp",EDGE,"E23.19.0");var subQ1=makeQuery(id+"F1.opRevolve","SWEPT_EDGE",EDGE,{"disambiguationData":[OSD([sQuery(id+"F0.wireOp",EDGE,"E12"),sQuery(id+"F0.wireOp",EDGE,"E21")])]});var subQ2=makeQuery(id+"F2.imprint","INTERSECT",VERTEX,{"disambiguationData":[OD(0.0)],"derivedFrom":[subQ1,subQ0]});Q47=makeQuery(id+"F2.imprint","IMPRINT",FACE,{"disambiguationData":[TD([[makeQuery(id+"F2.imprint","IMPRINT",EDGE,{"disambiguationData":[TD([[subQ2,1.0]])],"derivedFrom":subQ0}),1.0]])]});}
            var Q48;
            {var subQ0=sQuery(id+"F2.wireOp",EDGE,"E23.18.0");var subQ1=makeQuery(id+"F1.opRevolve","SWEPT_EDGE",EDGE,{"disambiguationData":[OSD([sQuery(id+"F0.wireOp",EDGE,"E12"),sQuery(id+"F0.wireOp",EDGE,"E21")])]});var subQ2=makeQuery(id+"F2.imprint","INTERSECT",VERTEX,{"disambiguationData":[OD(0.0)],"derivedFrom":[subQ1,subQ0]});Q48=makeQuery(id+"F2.imprint","IMPRINT",FACE,{"disambiguationData":[TD([[makeQuery(id+"F2.imprint","IMPRINT",EDGE,{"disambiguationData":[TD([[subQ2,-1.0]])],"derivedFrom":subQ0}),1.0]])]});}
            var Q49;
            {var subQ0=sQuery(id+"F2.wireOp",EDGE,"E23.18.0");var subQ1=makeQuery(id+"F1.opRevolve","SWEPT_EDGE",EDGE,{"disambiguationData":[OSD([sQuery(id+"F0.wireOp",EDGE,"E12"),sQuery(id+"F0.wireOp",EDGE,"E21")])]});var subQ2=makeQuery(id+"F2.imprint","INTERSECT",VERTEX,{"disambiguationData":[OD(0.0)],"derivedFrom":[subQ1,subQ0]});Q49=makeQuery(id+"F2.imprint","IMPRINT",FACE,{"disambiguationData":[TD([[makeQuery(id+"F2.imprint","IMPRINT",EDGE,{"disambiguationData":[TD([[subQ2,1.0]])],"derivedFrom":subQ0}),1.0]])]});}
            var Q50;
            {var subQ0=sQuery(id+"F2.wireOp",EDGE,"E23.23.0");var subQ1=makeQuery(id+"F1.opRevolve","SWEPT_EDGE",EDGE,{"disambiguationData":[OSD([sQuery(id+"F0.wireOp",EDGE,"E12"),sQuery(id+"F0.wireOp",EDGE,"E21")])]});var subQ2=makeQuery(id+"F2.imprint","INTERSECT",VERTEX,{"disambiguationData":[OD(0.0)],"derivedFrom":[subQ1,subQ0]});Q50=makeQuery(id+"F2.imprint","IMPRINT",FACE,{"disambiguationData":[TD([[makeQuery(id+"F2.imprint","IMPRINT",EDGE,{"disambiguationData":[TD([[subQ2,-1.0]])],"derivedFrom":subQ0}),1.0]])]});}
            var Q51;
            {var subQ0=sQuery(id+"F2.wireOp",EDGE,"E23.23.0");var subQ1=makeQuery(id+"F1.opRevolve","SWEPT_EDGE",EDGE,{"disambiguationData":[OSD([sQuery(id+"F0.wireOp",EDGE,"E12"),sQuery(id+"F0.wireOp",EDGE,"E21")])]});var subQ2=makeQuery(id+"F2.imprint","INTERSECT",VERTEX,{"disambiguationData":[OD(0.0)],"derivedFrom":[subQ1,subQ0]});Q51=makeQuery(id+"F2.imprint","IMPRINT",FACE,{"disambiguationData":[TD([[makeQuery(id+"F2.imprint","IMPRINT",EDGE,{"disambiguationData":[TD([[subQ2,1.0]])],"derivedFrom":subQ0}),1.0]])]});}
            var Q52;
            {var subQ0=sQuery(id+"F2.wireOp",EDGE,"E23.22.0");var subQ1=makeQuery(id+"F1.opRevolve","SWEPT_EDGE",EDGE,{"disambiguationData":[OSD([sQuery(id+"F0.wireOp",EDGE,"E12"),sQuery(id+"F0.wireOp",EDGE,"E21")])]});var subQ2=makeQuery(id+"F2.imprint","INTERSECT",VERTEX,{"disambiguationData":[OD(0.0)],"derivedFrom":[subQ1,subQ0]});Q52=makeQuery(id+"F2.imprint","IMPRINT",FACE,{"disambiguationData":[TD([[makeQuery(id+"F2.imprint","IMPRINT",EDGE,{"disambiguationData":[TD([[subQ2,-1.0]])],"derivedFrom":subQ0}),1.0]])]});}
            var Q53;
            {var subQ0=sQuery(id+"F2.wireOp",EDGE,"E23.22.0");var subQ1=makeQuery(id+"F1.opRevolve","SWEPT_EDGE",EDGE,{"disambiguationData":[OSD([sQuery(id+"F0.wireOp",EDGE,"E12"),sQuery(id+"F0.wireOp",EDGE,"E21")])]});var subQ2=makeQuery(id+"F2.imprint","INTERSECT",VERTEX,{"disambiguationData":[OD(0.0)],"derivedFrom":[subQ1,subQ0]});Q53=makeQuery(id+"F2.imprint","IMPRINT",FACE,{"disambiguationData":[TD([[makeQuery(id+"F2.imprint","IMPRINT",EDGE,{"disambiguationData":[TD([[subQ2,1.0]])],"derivedFrom":subQ0}),1.0]])]});}
            var Q54;
            {var subQ0=sQuery(id+"F2.wireOp",EDGE,"E23.21.0");var subQ1=makeQuery(id+"F1.opRevolve","SWEPT_EDGE",EDGE,{"disambiguationData":[OSD([sQuery(id+"F0.wireOp",EDGE,"E12"),sQuery(id+"F0.wireOp",EDGE,"E21")])]});var subQ2=makeQuery(id+"F2.imprint","INTERSECT",VERTEX,{"disambiguationData":[OD(0.0)],"derivedFrom":[subQ1,subQ0]});Q54=makeQuery(id+"F2.imprint","IMPRINT",FACE,{"disambiguationData":[TD([[makeQuery(id+"F2.imprint","IMPRINT",EDGE,{"disambiguationData":[TD([[subQ2,-1.0]])],"derivedFrom":subQ0}),1.0]])]});}
            var Q55;
            {var subQ0=sQuery(id+"F2.wireOp",EDGE,"E23.21.0");var subQ1=makeQuery(id+"F1.opRevolve","SWEPT_EDGE",EDGE,{"disambiguationData":[OSD([sQuery(id+"F0.wireOp",EDGE,"E12"),sQuery(id+"F0.wireOp",EDGE,"E21")])]});var subQ2=makeQuery(id+"F2.imprint","INTERSECT",VERTEX,{"disambiguationData":[OD(0.0)],"derivedFrom":[subQ1,subQ0]});Q55=makeQuery(id+"F2.imprint","IMPRINT",FACE,{"disambiguationData":[TD([[makeQuery(id+"F2.imprint","IMPRINT",EDGE,{"disambiguationData":[TD([[subQ2,1.0]])],"derivedFrom":subQ0}),1.0]])]});}
            var Q56;
            {var subQ0=sQuery(id+"F2.wireOp",EDGE,"E23.24.0");var subQ1=makeQuery(id+"F1.opRevolve","SWEPT_EDGE",EDGE,{"disambiguationData":[OSD([sQuery(id+"F0.wireOp",EDGE,"E12"),sQuery(id+"F0.wireOp",EDGE,"E21")])]});var subQ2=makeQuery(id+"F2.imprint","INTERSECT",VERTEX,{"disambiguationData":[OD(0.0)],"derivedFrom":[subQ1,subQ0]});Q56=makeQuery(id+"F2.imprint","IMPRINT",FACE,{"disambiguationData":[TD([[makeQuery(id+"F2.imprint","IMPRINT",EDGE,{"disambiguationData":[TD([[subQ2,1.0]])],"derivedFrom":subQ0}),1.0]])]});}
            var Q57;
            {var subQ0=sQuery(id+"F2.wireOp",EDGE,"E23.24.0");var subQ1=makeQuery(id+"F1.opRevolve","SWEPT_EDGE",EDGE,{"disambiguationData":[OSD([sQuery(id+"F0.wireOp",EDGE,"E12"),sQuery(id+"F0.wireOp",EDGE,"E21")])]});var subQ2=makeQuery(id+"F2.imprint","INTERSECT",VERTEX,{"disambiguationData":[OD(0.0)],"derivedFrom":[subQ1,subQ0]});Q57=makeQuery(id+"F2.imprint","IMPRINT",FACE,{"disambiguationData":[TD([[makeQuery(id+"F2.imprint","IMPRINT",EDGE,{"disambiguationData":[TD([[subQ2,-1.0]])],"derivedFrom":subQ0}),1.0]])]});}
            var Q58;
            {var subQ0=sQuery(id+"F2.wireOp",EDGE,"E23.25.0");var subQ1=makeQuery(id+"F1.opRevolve","SWEPT_EDGE",EDGE,{"disambiguationData":[OSD([sQuery(id+"F0.wireOp",EDGE,"E12"),sQuery(id+"F0.wireOp",EDGE,"E21")])]});var subQ2=makeQuery(id+"F2.imprint","INTERSECT",VERTEX,{"disambiguationData":[OD(0.0)],"derivedFrom":[subQ1,subQ0]});Q58=makeQuery(id+"F2.imprint","IMPRINT",FACE,{"disambiguationData":[TD([[makeQuery(id+"F2.imprint","IMPRINT",EDGE,{"disambiguationData":[TD([[subQ2,-1.0]])],"derivedFrom":subQ0}),1.0]])]});}
            var Q59;
            {var subQ0=sQuery(id+"F2.wireOp",EDGE,"E23.25.0");var subQ1=makeQuery(id+"F1.opRevolve","SWEPT_EDGE",EDGE,{"disambiguationData":[OSD([sQuery(id+"F0.wireOp",EDGE,"E12"),sQuery(id+"F0.wireOp",EDGE,"E21")])]});var subQ2=makeQuery(id+"F2.imprint","INTERSECT",VERTEX,{"disambiguationData":[OD(0.0)],"derivedFrom":[subQ1,subQ0]});Q59=makeQuery(id+"F2.imprint","IMPRINT",FACE,{"disambiguationData":[TD([[makeQuery(id+"F2.imprint","IMPRINT",EDGE,{"disambiguationData":[TD([[subQ2,1.0]])],"derivedFrom":subQ0}),1.0]])]});}
            var Q60;
            {var subQ0=sQuery(id+"F2.wireOp",EDGE,"E23.26.0");var subQ1=makeQuery(id+"F1.opRevolve","SWEPT_EDGE",EDGE,{"disambiguationData":[OSD([sQuery(id+"F0.wireOp",EDGE,"E12"),sQuery(id+"F0.wireOp",EDGE,"E21")])]});var subQ2=makeQuery(id+"F2.imprint","INTERSECT",VERTEX,{"disambiguationData":[OD(0.0)],"derivedFrom":[subQ1,subQ0]});Q60=makeQuery(id+"F2.imprint","IMPRINT",FACE,{"disambiguationData":[TD([[makeQuery(id+"F2.imprint","IMPRINT",EDGE,{"disambiguationData":[TD([[subQ2,1.0]])],"derivedFrom":subQ0}),1.0]])]});}
            var Q61;
            {var subQ0=sQuery(id+"F2.wireOp",EDGE,"E23.26.0");var subQ1=makeQuery(id+"F1.opRevolve","SWEPT_EDGE",EDGE,{"disambiguationData":[OSD([sQuery(id+"F0.wireOp",EDGE,"E12"),sQuery(id+"F0.wireOp",EDGE,"E21")])]});var subQ2=makeQuery(id+"F2.imprint","INTERSECT",VERTEX,{"disambiguationData":[OD(0.0)],"derivedFrom":[subQ1,subQ0]});Q61=makeQuery(id+"F2.imprint","IMPRINT",FACE,{"disambiguationData":[TD([[makeQuery(id+"F2.imprint","IMPRINT",EDGE,{"disambiguationData":[TD([[subQ2,-1.0]])],"derivedFrom":subQ0}),1.0]])]});}
            var Q62;
            {var subQ0=sQuery(id+"F2.wireOp",EDGE,"E23.27.0");var subQ1=makeQuery(id+"F1.opRevolve","SWEPT_EDGE",EDGE,{"disambiguationData":[OSD([sQuery(id+"F0.wireOp",EDGE,"E12"),sQuery(id+"F0.wireOp",EDGE,"E21")])]});var subQ2=makeQuery(id+"F2.imprint","INTERSECT",VERTEX,{"disambiguationData":[OD(0.0)],"derivedFrom":[subQ1,subQ0]});Q62=makeQuery(id+"F2.imprint","IMPRINT",FACE,{"disambiguationData":[TD([[makeQuery(id+"F2.imprint","IMPRINT",EDGE,{"disambiguationData":[TD([[subQ2,-1.0]])],"derivedFrom":subQ0}),1.0]])]});}
            var Q63;
            {var subQ0=sQuery(id+"F2.wireOp",EDGE,"E23.27.0");var subQ1=makeQuery(id+"F1.opRevolve","SWEPT_EDGE",EDGE,{"disambiguationData":[OSD([sQuery(id+"F0.wireOp",EDGE,"E12"),sQuery(id+"F0.wireOp",EDGE,"E21")])]});var subQ2=makeQuery(id+"F2.imprint","INTERSECT",VERTEX,{"disambiguationData":[OD(0.0)],"derivedFrom":[subQ1,subQ0]});Q63=makeQuery(id+"F2.imprint","IMPRINT",FACE,{"disambiguationData":[TD([[makeQuery(id+"F2.imprint","IMPRINT",EDGE,{"disambiguationData":[TD([[subQ2,1.0]])],"derivedFrom":subQ0}),1.0]])]});}
            var Q64;
            {var subQ0=sQuery(id+"F2.wireOp",EDGE,"E23.28.0");var subQ1=makeQuery(id+"F1.opRevolve","SWEPT_EDGE",EDGE,{"disambiguationData":[OSD([sQuery(id+"F0.wireOp",EDGE,"E12"),sQuery(id+"F0.wireOp",EDGE,"E21")])]});var subQ2=makeQuery(id+"F2.imprint","INTERSECT",VERTEX,{"disambiguationData":[OD(0.0)],"derivedFrom":[subQ1,subQ0]});Q64=makeQuery(id+"F2.imprint","IMPRINT",FACE,{"disambiguationData":[TD([[makeQuery(id+"F2.imprint","IMPRINT",EDGE,{"disambiguationData":[TD([[subQ2,-1.0]])],"derivedFrom":subQ0}),1.0]])]});}
            var Q65;
            {var subQ0=sQuery(id+"F2.wireOp",EDGE,"E23.28.0");var subQ1=makeQuery(id+"F1.opRevolve","SWEPT_EDGE",EDGE,{"disambiguationData":[OSD([sQuery(id+"F0.wireOp",EDGE,"E12"),sQuery(id+"F0.wireOp",EDGE,"E21")])]});var subQ2=makeQuery(id+"F2.imprint","INTERSECT",VERTEX,{"disambiguationData":[OD(0.0)],"derivedFrom":[subQ1,subQ0]});Q65=makeQuery(id+"F2.imprint","IMPRINT",FACE,{"disambiguationData":[TD([[makeQuery(id+"F2.imprint","IMPRINT",EDGE,{"disambiguationData":[TD([[subQ2,1.0]])],"derivedFrom":subQ0}),1.0]])]});}
            var Q66;
            {var subQ0=sQuery(id+"F2.wireOp",EDGE,"E23.29.0");var subQ1=makeQuery(id+"F1.opRevolve","SWEPT_EDGE",EDGE,{"disambiguationData":[OSD([sQuery(id+"F0.wireOp",EDGE,"E12"),sQuery(id+"F0.wireOp",EDGE,"E21")])]});var subQ2=makeQuery(id+"F2.imprint","INTERSECT",VERTEX,{"disambiguationData":[OD(0.0)],"derivedFrom":[subQ1,subQ0]});Q66=makeQuery(id+"F2.imprint","IMPRINT",FACE,{"disambiguationData":[TD([[makeQuery(id+"F2.imprint","IMPRINT",EDGE,{"disambiguationData":[TD([[subQ2,1.0]])],"derivedFrom":subQ0}),1.0]])]});}
            var Q67;
            {var subQ0=sQuery(id+"F2.wireOp",EDGE,"E23.29.0");var subQ1=makeQuery(id+"F1.opRevolve","SWEPT_EDGE",EDGE,{"disambiguationData":[OSD([sQuery(id+"F0.wireOp",EDGE,"E12"),sQuery(id+"F0.wireOp",EDGE,"E21")])]});var subQ2=makeQuery(id+"F2.imprint","INTERSECT",VERTEX,{"disambiguationData":[OD(0.0)],"derivedFrom":[subQ1,subQ0]});Q67=makeQuery(id+"F2.imprint","IMPRINT",FACE,{"disambiguationData":[TD([[makeQuery(id+"F2.imprint","IMPRINT",EDGE,{"disambiguationData":[TD([[subQ2,-1.0]])],"derivedFrom":subQ0}),1.0]])]});}
            var Q68;
            {var subQ0=sQuery(id+"F2.wireOp",EDGE,"E23.30.0");var subQ1=makeQuery(id+"F1.opRevolve","SWEPT_EDGE",EDGE,{"disambiguationData":[OSD([sQuery(id+"F0.wireOp",EDGE,"E12"),sQuery(id+"F0.wireOp",EDGE,"E21")])]});var subQ2=makeQuery(id+"F2.imprint","INTERSECT",VERTEX,{"disambiguationData":[OD(0.0)],"derivedFrom":[subQ1,subQ0]});Q68=makeQuery(id+"F2.imprint","IMPRINT",FACE,{"disambiguationData":[TD([[makeQuery(id+"F2.imprint","IMPRINT",EDGE,{"disambiguationData":[TD([[subQ2,1.0]])],"derivedFrom":subQ0}),1.0]])]});}
            var Q69;
            {var subQ0=sQuery(id+"F2.wireOp",EDGE,"E23.30.0");var subQ1=makeQuery(id+"F1.opRevolve","SWEPT_EDGE",EDGE,{"disambiguationData":[OSD([sQuery(id+"F0.wireOp",EDGE,"E12"),sQuery(id+"F0.wireOp",EDGE,"E21")])]});var subQ2=makeQuery(id+"F2.imprint","INTERSECT",VERTEX,{"disambiguationData":[OD(0.0)],"derivedFrom":[subQ1,subQ0]});Q69=makeQuery(id+"F2.imprint","IMPRINT",FACE,{"disambiguationData":[TD([[makeQuery(id+"F2.imprint","IMPRINT",EDGE,{"disambiguationData":[TD([[subQ2,-1.0]])],"derivedFrom":subQ0}),1.0]])]});}
            var Q70;
            {var subQ0=sQuery(id+"F2.wireOp",EDGE,"E23.31.0");var subQ1=makeQuery(id+"F1.opRevolve","SWEPT_EDGE",EDGE,{"disambiguationData":[OSD([sQuery(id+"F0.wireOp",EDGE,"E12"),sQuery(id+"F0.wireOp",EDGE,"E21")])]});var subQ2=makeQuery(id+"F2.imprint","INTERSECT",VERTEX,{"disambiguationData":[OD(0.0)],"derivedFrom":[subQ1,subQ0]});Q70=makeQuery(id+"F2.imprint","IMPRINT",FACE,{"disambiguationData":[TD([[makeQuery(id+"F2.imprint","IMPRINT",EDGE,{"disambiguationData":[TD([[subQ2,1.0]])],"derivedFrom":subQ0}),1.0]])]});}
            var Q71;
            {var subQ0=sQuery(id+"F2.wireOp",EDGE,"E23.31.0");var subQ1=makeQuery(id+"F1.opRevolve","SWEPT_EDGE",EDGE,{"disambiguationData":[OSD([sQuery(id+"F0.wireOp",EDGE,"E12"),sQuery(id+"F0.wireOp",EDGE,"E21")])]});var subQ2=makeQuery(id+"F2.imprint","INTERSECT",VERTEX,{"disambiguationData":[OD(0.0)],"derivedFrom":[subQ1,subQ0]});Q71=makeQuery(id+"F2.imprint","IMPRINT",FACE,{"disambiguationData":[TD([[makeQuery(id+"F2.imprint","IMPRINT",EDGE,{"disambiguationData":[TD([[subQ2,-1.0]])],"derivedFrom":subQ0}),1.0]])]});}
            var Q72;
            {var subQ0=sQuery(id+"F2.wireOp",EDGE,"E23.32.0");var subQ1=makeQuery(id+"F1.opRevolve","SWEPT_EDGE",EDGE,{"disambiguationData":[OSD([sQuery(id+"F0.wireOp",EDGE,"E12"),sQuery(id+"F0.wireOp",EDGE,"E21")])]});var subQ2=makeQuery(id+"F2.imprint","INTERSECT",VERTEX,{"disambiguationData":[OD(0.0)],"derivedFrom":[subQ1,subQ0]});Q72=makeQuery(id+"F2.imprint","IMPRINT",FACE,{"disambiguationData":[TD([[makeQuery(id+"F2.imprint","IMPRINT",EDGE,{"disambiguationData":[TD([[subQ2,1.0]])],"derivedFrom":subQ0}),1.0]])]});}
            var Q73;
            {var subQ0=sQuery(id+"F2.wireOp",EDGE,"E23.32.0");var subQ1=makeQuery(id+"F1.opRevolve","SWEPT_EDGE",EDGE,{"disambiguationData":[OSD([sQuery(id+"F0.wireOp",EDGE,"E12"),sQuery(id+"F0.wireOp",EDGE,"E21")])]});var subQ2=makeQuery(id+"F2.imprint","INTERSECT",VERTEX,{"disambiguationData":[OD(0.0)],"derivedFrom":[subQ1,subQ0]});Q73=makeQuery(id+"F2.imprint","IMPRINT",FACE,{"disambiguationData":[TD([[makeQuery(id+"F2.imprint","IMPRINT",EDGE,{"disambiguationData":[TD([[subQ2,-1.0]])],"derivedFrom":subQ0}),1.0]])]});}
            var Q74;
            {var subQ0=sQuery(id+"F2.wireOp",EDGE,"E23.33.0");var subQ1=makeQuery(id+"F1.opRevolve","SWEPT_EDGE",EDGE,{"disambiguationData":[OSD([sQuery(id+"F0.wireOp",EDGE,"E12"),sQuery(id+"F0.wireOp",EDGE,"E21")])]});var subQ2=makeQuery(id+"F2.imprint","INTERSECT",VERTEX,{"disambiguationData":[OD(0.0)],"derivedFrom":[subQ1,subQ0]});Q74=makeQuery(id+"F2.imprint","IMPRINT",FACE,{"disambiguationData":[TD([[makeQuery(id+"F2.imprint","IMPRINT",EDGE,{"disambiguationData":[TD([[subQ2,1.0]])],"derivedFrom":subQ0}),1.0]])]});}
            var Q75;
            {var subQ0=sQuery(id+"F2.wireOp",EDGE,"E23.33.0");var subQ1=makeQuery(id+"F1.opRevolve","SWEPT_EDGE",EDGE,{"disambiguationData":[OSD([sQuery(id+"F0.wireOp",EDGE,"E12"),sQuery(id+"F0.wireOp",EDGE,"E21")])]});var subQ2=makeQuery(id+"F2.imprint","INTERSECT",VERTEX,{"disambiguationData":[OD(0.0)],"derivedFrom":[subQ1,subQ0]});Q75=makeQuery(id+"F2.imprint","IMPRINT",FACE,{"disambiguationData":[TD([[makeQuery(id+"F2.imprint","IMPRINT",EDGE,{"disambiguationData":[TD([[subQ2,-1.0]])],"derivedFrom":subQ0}),1.0]])]});}
            var Q76;
            {var subQ0=sQuery(id+"F2.wireOp",EDGE,"E23.34.0");var subQ1=makeQuery(id+"F1.opRevolve","SWEPT_EDGE",EDGE,{"disambiguationData":[OSD([sQuery(id+"F0.wireOp",EDGE,"E12"),sQuery(id+"F0.wireOp",EDGE,"E21")])]});var subQ2=makeQuery(id+"F2.imprint","INTERSECT",VERTEX,{"disambiguationData":[OD(0.0)],"derivedFrom":[subQ1,subQ0]});Q76=makeQuery(id+"F2.imprint","IMPRINT",FACE,{"disambiguationData":[TD([[makeQuery(id+"F2.imprint","IMPRINT",EDGE,{"disambiguationData":[TD([[subQ2,-1.0]])],"derivedFrom":subQ0}),1.0]])]});}
            var Q77;
            {var subQ0=sQuery(id+"F2.wireOp",EDGE,"E23.34.0");var subQ1=makeQuery(id+"F1.opRevolve","SWEPT_EDGE",EDGE,{"disambiguationData":[OSD([sQuery(id+"F0.wireOp",EDGE,"E12"),sQuery(id+"F0.wireOp",EDGE,"E21")])]});var subQ2=makeQuery(id+"F2.imprint","INTERSECT",VERTEX,{"disambiguationData":[OD(0.0)],"derivedFrom":[subQ1,subQ0]});Q77=makeQuery(id+"F2.imprint","IMPRINT",FACE,{"disambiguationData":[TD([[makeQuery(id+"F2.imprint","IMPRINT",EDGE,{"disambiguationData":[TD([[subQ2,1.0]])],"derivedFrom":subQ0}),1.0]])]});}
            var Q78;
            {var subQ0=sQuery(id+"F2.wireOp",EDGE,"E23.45.0");var subQ1=makeQuery(id+"F1.opRevolve","SWEPT_EDGE",EDGE,{"disambiguationData":[OSD([sQuery(id+"F0.wireOp",EDGE,"E12"),sQuery(id+"F0.wireOp",EDGE,"E21")])]});var subQ2=makeQuery(id+"F2.imprint","INTERSECT",VERTEX,{"disambiguationData":[OD(0.0)],"derivedFrom":[subQ1,subQ0]});Q78=makeQuery(id+"F2.imprint","IMPRINT",FACE,{"disambiguationData":[TD([[makeQuery(id+"F2.imprint","IMPRINT",EDGE,{"disambiguationData":[TD([[subQ2,1.0]])],"derivedFrom":subQ0}),1.0]])]});}
            var Q79;
            {var subQ0=sQuery(id+"F2.wireOp",EDGE,"E23.45.0");var subQ1=makeQuery(id+"F1.opRevolve","SWEPT_EDGE",EDGE,{"disambiguationData":[OSD([sQuery(id+"F0.wireOp",EDGE,"E12"),sQuery(id+"F0.wireOp",EDGE,"E21")])]});var subQ2=makeQuery(id+"F2.imprint","INTERSECT",VERTEX,{"disambiguationData":[OD(0.0)],"derivedFrom":[subQ1,subQ0]});Q79=makeQuery(id+"F2.imprint","IMPRINT",FACE,{"disambiguationData":[TD([[makeQuery(id+"F2.imprint","IMPRINT",EDGE,{"disambiguationData":[TD([[subQ2,-1.0]])],"derivedFrom":subQ0}),1.0]])]});}
            var Q80;
            {var subQ0=sQuery(id+"F2.wireOp",EDGE,"E23.44.0");var subQ1=makeQuery(id+"F1.opRevolve","SWEPT_EDGE",EDGE,{"disambiguationData":[OSD([sQuery(id+"F0.wireOp",EDGE,"E12"),sQuery(id+"F0.wireOp",EDGE,"E21")])]});var subQ2=makeQuery(id+"F2.imprint","INTERSECT",VERTEX,{"disambiguationData":[OD(0.0)],"derivedFrom":[subQ1,subQ0]});Q80=makeQuery(id+"F2.imprint","IMPRINT",FACE,{"disambiguationData":[TD([[makeQuery(id+"F2.imprint","IMPRINT",EDGE,{"disambiguationData":[TD([[subQ2,1.0]])],"derivedFrom":subQ0}),1.0]])]});}
            var Q81;
            {var subQ0=sQuery(id+"F2.wireOp",EDGE,"E23.44.0");var subQ1=makeQuery(id+"F1.opRevolve","SWEPT_EDGE",EDGE,{"disambiguationData":[OSD([sQuery(id+"F0.wireOp",EDGE,"E12"),sQuery(id+"F0.wireOp",EDGE,"E21")])]});var subQ2=makeQuery(id+"F2.imprint","INTERSECT",VERTEX,{"disambiguationData":[OD(0.0)],"derivedFrom":[subQ1,subQ0]});Q81=makeQuery(id+"F2.imprint","IMPRINT",FACE,{"disambiguationData":[TD([[makeQuery(id+"F2.imprint","IMPRINT",EDGE,{"disambiguationData":[TD([[subQ2,-1.0]])],"derivedFrom":subQ0}),1.0]])]});}
            var Q82;
            {var subQ0=sQuery(id+"F2.wireOp",EDGE,"E23.41.0");var subQ1=makeQuery(id+"F1.opRevolve","SWEPT_EDGE",EDGE,{"disambiguationData":[OSD([sQuery(id+"F0.wireOp",EDGE,"E12"),sQuery(id+"F0.wireOp",EDGE,"E21")])]});var subQ2=makeQuery(id+"F2.imprint","INTERSECT",VERTEX,{"disambiguationData":[OD(0.0)],"derivedFrom":[subQ1,subQ0]});Q82=makeQuery(id+"F2.imprint","IMPRINT",FACE,{"disambiguationData":[TD([[makeQuery(id+"F2.imprint","IMPRINT",EDGE,{"disambiguationData":[TD([[subQ2,-1.0]])],"derivedFrom":subQ0}),1.0]])]});}
            var Q83;
            {var subQ0=sQuery(id+"F2.wireOp",EDGE,"E23.41.0");var subQ1=makeQuery(id+"F1.opRevolve","SWEPT_EDGE",EDGE,{"disambiguationData":[OSD([sQuery(id+"F0.wireOp",EDGE,"E12"),sQuery(id+"F0.wireOp",EDGE,"E21")])]});var subQ2=makeQuery(id+"F2.imprint","INTERSECT",VERTEX,{"disambiguationData":[OD(0.0)],"derivedFrom":[subQ1,subQ0]});Q83=makeQuery(id+"F2.imprint","IMPRINT",FACE,{"disambiguationData":[TD([[makeQuery(id+"F2.imprint","IMPRINT",EDGE,{"disambiguationData":[TD([[subQ2,1.0]])],"derivedFrom":subQ0}),1.0]])]});}
            var Q84;
            {var subQ0=sQuery(id+"F2.wireOp",EDGE,"E23.42.0");var subQ1=makeQuery(id+"F1.opRevolve","SWEPT_EDGE",EDGE,{"disambiguationData":[OSD([sQuery(id+"F0.wireOp",EDGE,"E12"),sQuery(id+"F0.wireOp",EDGE,"E21")])]});var subQ2=makeQuery(id+"F2.imprint","INTERSECT",VERTEX,{"disambiguationData":[OD(0.0)],"derivedFrom":[subQ1,subQ0]});Q84=makeQuery(id+"F2.imprint","IMPRINT",FACE,{"disambiguationData":[TD([[makeQuery(id+"F2.imprint","IMPRINT",EDGE,{"disambiguationData":[TD([[subQ2,-1.0]])],"derivedFrom":subQ0}),1.0]])]});}
            var Q85;
            {var subQ0=sQuery(id+"F2.wireOp",EDGE,"E23.42.0");var subQ1=makeQuery(id+"F1.opRevolve","SWEPT_EDGE",EDGE,{"disambiguationData":[OSD([sQuery(id+"F0.wireOp",EDGE,"E12"),sQuery(id+"F0.wireOp",EDGE,"E21")])]});var subQ2=makeQuery(id+"F2.imprint","INTERSECT",VERTEX,{"disambiguationData":[OD(0.0)],"derivedFrom":[subQ1,subQ0]});Q85=makeQuery(id+"F2.imprint","IMPRINT",FACE,{"disambiguationData":[TD([[makeQuery(id+"F2.imprint","IMPRINT",EDGE,{"disambiguationData":[TD([[subQ2,1.0]])],"derivedFrom":subQ0}),1.0]])]});}
            var Q86;
            {var subQ0=sQuery(id+"F2.wireOp",EDGE,"E23.43.0");var subQ1=makeQuery(id+"F1.opRevolve","SWEPT_EDGE",EDGE,{"disambiguationData":[OSD([sQuery(id+"F0.wireOp",EDGE,"E12"),sQuery(id+"F0.wireOp",EDGE,"E21")])]});var subQ2=makeQuery(id+"F2.imprint","INTERSECT",VERTEX,{"disambiguationData":[OD(0.0)],"derivedFrom":[subQ1,subQ0]});Q86=makeQuery(id+"F2.imprint","IMPRINT",FACE,{"disambiguationData":[TD([[makeQuery(id+"F2.imprint","IMPRINT",EDGE,{"disambiguationData":[TD([[subQ2,-1.0]])],"derivedFrom":subQ0}),1.0]])]});}
            var Q87;
            {var subQ0=sQuery(id+"F2.wireOp",EDGE,"E23.43.0");var subQ1=makeQuery(id+"F1.opRevolve","SWEPT_EDGE",EDGE,{"disambiguationData":[OSD([sQuery(id+"F0.wireOp",EDGE,"E12"),sQuery(id+"F0.wireOp",EDGE,"E21")])]});var subQ2=makeQuery(id+"F2.imprint","INTERSECT",VERTEX,{"disambiguationData":[OD(0.0)],"derivedFrom":[subQ1,subQ0]});Q87=makeQuery(id+"F2.imprint","IMPRINT",FACE,{"disambiguationData":[TD([[makeQuery(id+"F2.imprint","IMPRINT",EDGE,{"disambiguationData":[TD([[subQ2,1.0]])],"derivedFrom":subQ0}),1.0]])]});}
            var Q88;
            {var subQ0=sQuery(id+"F2.wireOp",EDGE,"E23.40.0");var subQ1=makeQuery(id+"F1.opRevolve","SWEPT_EDGE",EDGE,{"disambiguationData":[OSD([sQuery(id+"F0.wireOp",EDGE,"E12"),sQuery(id+"F0.wireOp",EDGE,"E21")])]});var subQ2=makeQuery(id+"F2.imprint","INTERSECT",VERTEX,{"disambiguationData":[OD(0.0)],"derivedFrom":[subQ1,subQ0]});Q88=makeQuery(id+"F2.imprint","IMPRINT",FACE,{"disambiguationData":[TD([[makeQuery(id+"F2.imprint","IMPRINT",EDGE,{"disambiguationData":[TD([[subQ2,1.0]])],"derivedFrom":subQ0}),1.0]])]});}
            var Q89;
            {var subQ0=sQuery(id+"F2.wireOp",EDGE,"E23.40.0");var subQ1=makeQuery(id+"F1.opRevolve","SWEPT_EDGE",EDGE,{"disambiguationData":[OSD([sQuery(id+"F0.wireOp",EDGE,"E12"),sQuery(id+"F0.wireOp",EDGE,"E21")])]});var subQ2=makeQuery(id+"F2.imprint","INTERSECT",VERTEX,{"disambiguationData":[OD(0.0)],"derivedFrom":[subQ1,subQ0]});Q89=makeQuery(id+"F2.imprint","IMPRINT",FACE,{"disambiguationData":[TD([[makeQuery(id+"F2.imprint","IMPRINT",EDGE,{"disambiguationData":[TD([[subQ2,-1.0]])],"derivedFrom":subQ0}),1.0]])]});}
            var Q90;
            {var subQ0=sQuery(id+"F2.wireOp",EDGE,"E23.39.0");var subQ1=makeQuery(id+"F1.opRevolve","SWEPT_EDGE",EDGE,{"disambiguationData":[OSD([sQuery(id+"F0.wireOp",EDGE,"E12"),sQuery(id+"F0.wireOp",EDGE,"E21")])]});var subQ2=makeQuery(id+"F2.imprint","INTERSECT",VERTEX,{"disambiguationData":[OD(0.0)],"derivedFrom":[subQ1,subQ0]});Q90=makeQuery(id+"F2.imprint","IMPRINT",FACE,{"disambiguationData":[TD([[makeQuery(id+"F2.imprint","IMPRINT",EDGE,{"disambiguationData":[TD([[subQ2,1.0]])],"derivedFrom":subQ0}),1.0]])]});}
            var Q91;
            {var subQ0=sQuery(id+"F2.wireOp",EDGE,"E23.39.0");var subQ1=makeQuery(id+"F1.opRevolve","SWEPT_EDGE",EDGE,{"disambiguationData":[OSD([sQuery(id+"F0.wireOp",EDGE,"E12"),sQuery(id+"F0.wireOp",EDGE,"E21")])]});var subQ2=makeQuery(id+"F2.imprint","INTERSECT",VERTEX,{"disambiguationData":[OD(0.0)],"derivedFrom":[subQ1,subQ0]});Q91=makeQuery(id+"F2.imprint","IMPRINT",FACE,{"disambiguationData":[TD([[makeQuery(id+"F2.imprint","IMPRINT",EDGE,{"disambiguationData":[TD([[subQ2,-1.0]])],"derivedFrom":subQ0}),1.0]])]});}
            var Q92;
            {var subQ0=sQuery(id+"F2.wireOp",EDGE,"E23.35.0");var subQ1=makeQuery(id+"F1.opRevolve","SWEPT_EDGE",EDGE,{"disambiguationData":[OSD([sQuery(id+"F0.wireOp",EDGE,"E12"),sQuery(id+"F0.wireOp",EDGE,"E21")])]});var subQ2=makeQuery(id+"F2.imprint","INTERSECT",VERTEX,{"disambiguationData":[OD(0.0)],"derivedFrom":[subQ1,subQ0]});Q92=makeQuery(id+"F2.imprint","IMPRINT",FACE,{"disambiguationData":[TD([[makeQuery(id+"F2.imprint","IMPRINT",EDGE,{"disambiguationData":[TD([[subQ2,1.0]])],"derivedFrom":subQ0}),1.0]])]});}
            var Q93;
            {var subQ0=sQuery(id+"F2.wireOp",EDGE,"E23.35.0");var subQ1=makeQuery(id+"F1.opRevolve","SWEPT_EDGE",EDGE,{"disambiguationData":[OSD([sQuery(id+"F0.wireOp",EDGE,"E12"),sQuery(id+"F0.wireOp",EDGE,"E21")])]});var subQ2=makeQuery(id+"F2.imprint","INTERSECT",VERTEX,{"disambiguationData":[OD(0.0)],"derivedFrom":[subQ1,subQ0]});Q93=makeQuery(id+"F2.imprint","IMPRINT",FACE,{"disambiguationData":[TD([[makeQuery(id+"F2.imprint","IMPRINT",EDGE,{"disambiguationData":[TD([[subQ2,-1.0]])],"derivedFrom":subQ0}),1.0]])]});}
            var Q94;
            {var subQ0=sQuery(id+"F2.wireOp",EDGE,"E23.36.0");var subQ1=makeQuery(id+"F1.opRevolve","SWEPT_EDGE",EDGE,{"disambiguationData":[OSD([sQuery(id+"F0.wireOp",EDGE,"E12"),sQuery(id+"F0.wireOp",EDGE,"E21")])]});var subQ2=makeQuery(id+"F2.imprint","INTERSECT",VERTEX,{"disambiguationData":[OD(0.0)],"derivedFrom":[subQ1,subQ0]});Q94=makeQuery(id+"F2.imprint","IMPRINT",FACE,{"disambiguationData":[TD([[makeQuery(id+"F2.imprint","IMPRINT",EDGE,{"disambiguationData":[TD([[subQ2,1.0]])],"derivedFrom":subQ0}),1.0]])]});}
            var Q95;
            {var subQ0=sQuery(id+"F2.wireOp",EDGE,"E23.36.0");var subQ1=makeQuery(id+"F1.opRevolve","SWEPT_EDGE",EDGE,{"disambiguationData":[OSD([sQuery(id+"F0.wireOp",EDGE,"E12"),sQuery(id+"F0.wireOp",EDGE,"E21")])]});var subQ2=makeQuery(id+"F2.imprint","INTERSECT",VERTEX,{"disambiguationData":[OD(0.0)],"derivedFrom":[subQ1,subQ0]});Q95=makeQuery(id+"F2.imprint","IMPRINT",FACE,{"disambiguationData":[TD([[makeQuery(id+"F2.imprint","IMPRINT",EDGE,{"disambiguationData":[TD([[subQ2,-1.0]])],"derivedFrom":subQ0}),1.0]])]});}
            var Q96;
            {var subQ0=sQuery(id+"F2.wireOp",EDGE,"E23.37.0");var subQ1=makeQuery(id+"F1.opRevolve","SWEPT_EDGE",EDGE,{"disambiguationData":[OSD([sQuery(id+"F0.wireOp",EDGE,"E12"),sQuery(id+"F0.wireOp",EDGE,"E21")])]});var subQ2=makeQuery(id+"F2.imprint","INTERSECT",VERTEX,{"disambiguationData":[OD(0.0)],"derivedFrom":[subQ1,subQ0]});Q96=makeQuery(id+"F2.imprint","IMPRINT",FACE,{"disambiguationData":[TD([[makeQuery(id+"F2.imprint","IMPRINT",EDGE,{"disambiguationData":[TD([[subQ2,-1.0]])],"derivedFrom":subQ0}),1.0]])]});}
            var Q97;
            {var subQ0=sQuery(id+"F2.wireOp",EDGE,"E23.37.0");var subQ1=makeQuery(id+"F1.opRevolve","SWEPT_EDGE",EDGE,{"disambiguationData":[OSD([sQuery(id+"F0.wireOp",EDGE,"E12"),sQuery(id+"F0.wireOp",EDGE,"E21")])]});var subQ2=makeQuery(id+"F2.imprint","INTERSECT",VERTEX,{"disambiguationData":[OD(0.0)],"derivedFrom":[subQ1,subQ0]});Q97=makeQuery(id+"F2.imprint","IMPRINT",FACE,{"disambiguationData":[TD([[makeQuery(id+"F2.imprint","IMPRINT",EDGE,{"disambiguationData":[TD([[subQ2,1.0]])],"derivedFrom":subQ0}),1.0]])]});}
            var Q98;
            {var subQ0=sQuery(id+"F2.wireOp",EDGE,"E23.38.0");var subQ1=makeQuery(id+"F1.opRevolve","SWEPT_EDGE",EDGE,{"disambiguationData":[OSD([sQuery(id+"F0.wireOp",EDGE,"E12"),sQuery(id+"F0.wireOp",EDGE,"E21")])]});var subQ2=makeQuery(id+"F2.imprint","INTERSECT",VERTEX,{"disambiguationData":[OD(0.0)],"derivedFrom":[subQ1,subQ0]});Q98=makeQuery(id+"F2.imprint","IMPRINT",FACE,{"disambiguationData":[TD([[makeQuery(id+"F2.imprint","IMPRINT",EDGE,{"disambiguationData":[TD([[subQ2,-1.0]])],"derivedFrom":subQ0}),1.0]])]});}
            var Q99;
            {var subQ0=sQuery(id+"F2.wireOp",EDGE,"E23.38.0");var subQ1=makeQuery(id+"F1.opRevolve","SWEPT_EDGE",EDGE,{"disambiguationData":[OSD([sQuery(id+"F0.wireOp",EDGE,"E12"),sQuery(id+"F0.wireOp",EDGE,"E21")])]});var subQ2=makeQuery(id+"F2.imprint","INTERSECT",VERTEX,{"disambiguationData":[OD(0.0)],"derivedFrom":[subQ1,subQ0]});Q99=makeQuery(id+"F2.imprint","IMPRINT",FACE,{"disambiguationData":[TD([[makeQuery(id+"F2.imprint","IMPRINT",EDGE,{"disambiguationData":[TD([[subQ2,1.0]])],"derivedFrom":subQ0}),1.0]])]});}
            var Q100;
            Q100=sQuery(id+"F2.wireOp",EDGE,"E23.46.0");
            extrude(context, id + "F3", {"entities" : qUnion([Q0, Q1, Q2, Q3, Q4, Q5, Q6, Q7, Q8, Q9, Q10, Q11, Q12, Q13, Q14, Q15, Q16, Q17, Q18, Q19, Q20, Q21, Q22, Q23, Q24, Q25, Q26, Q27, Q28, Q29, Q30, Q31, Q32, Q33, Q34, Q35, Q36, Q37, Q38, Q39, Q40, Q41, Q42, Q43, Q44, Q45, Q46, Q47, Q48, Q49, Q50, Q51, Q52, Q53, Q54, Q55, Q56, Q57, Q58, Q59, Q60, Q61, Q62, Q63, Q64, Q65, Q66, Q67, Q68, Q69, Q70, Q71, Q72, Q73, Q74, Q75, Q76, Q77, Q78, Q79, Q80, Q81, Q82, Q83, Q84, Q85, Q86, Q87, Q88, Q89, Q90, Q91, Q92, Q93, Q94, Q95, Q96, Q97, Q98, Q99]), "operationType" : NewBodyOperationType.ADD, "surfaceEntities" : qUnion([Q100]), "oppositeDirection" : true, "depth" : 97 * mm});
        }
        {
            var Q0;
            Q0=makeQuery(id+"F1.opRevolve","SWEPT_EDGE",EDGE,{"disambiguationData":[OSD([sQuery(id+"F0.wireOp",EDGE,"E8"),sQuery(id+"F0.wireOp",EDGE,"E9")])]});
            chamfer(context, id + "F4", {"entities" : qUnion([Q0]), "width" : 1 * mm, "tangentPropagation" : true});
        }
    });
